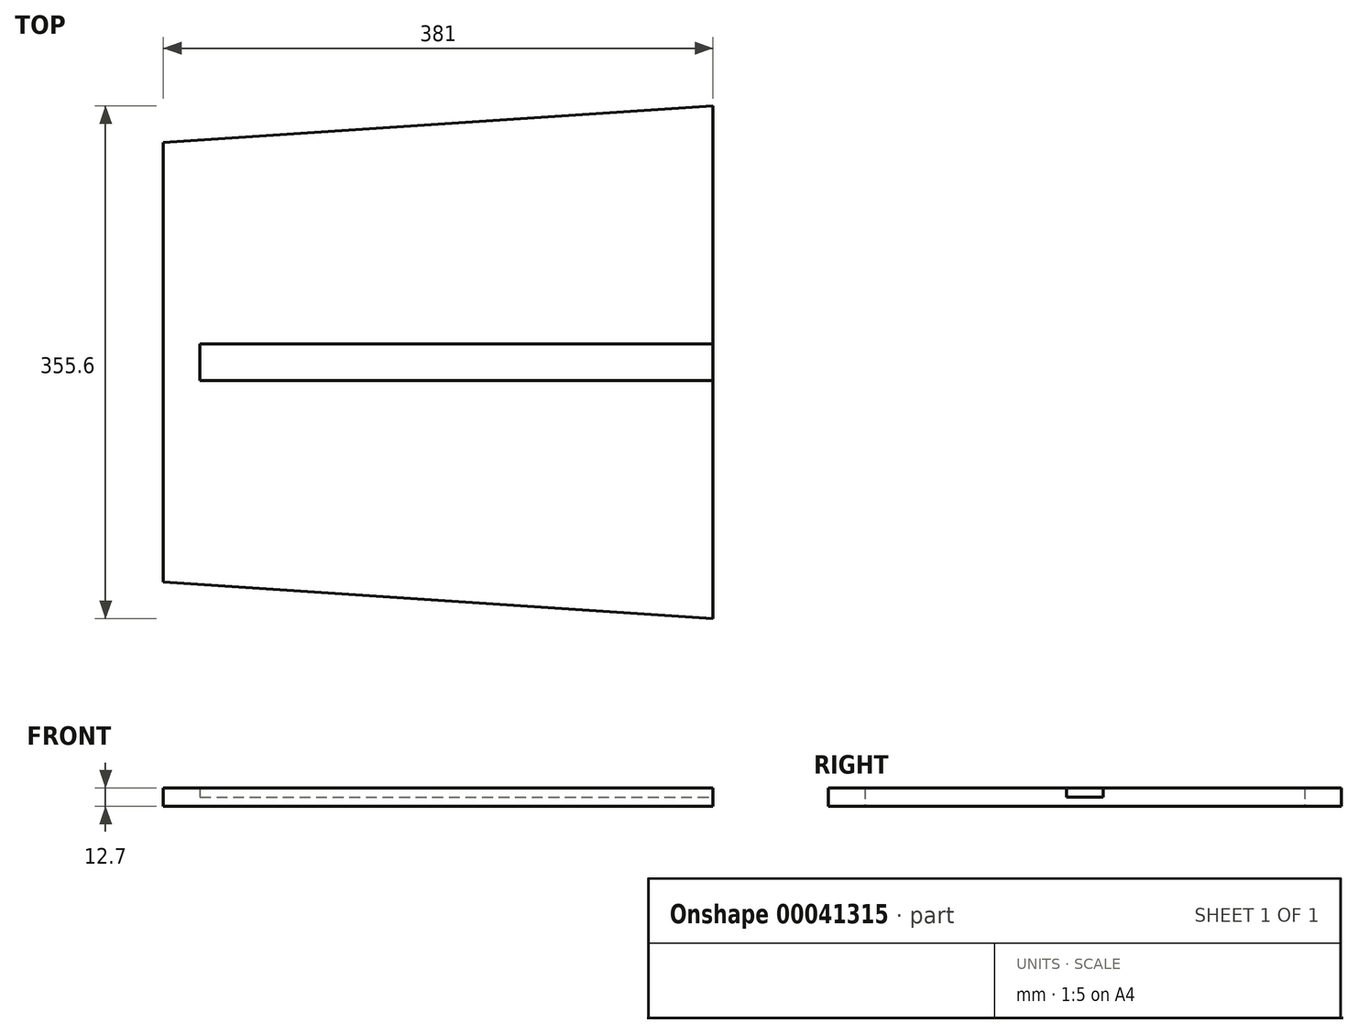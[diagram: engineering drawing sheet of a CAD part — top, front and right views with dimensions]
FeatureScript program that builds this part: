
annotation { "Feature Type Name" : "Feature", "Feature Type Description" : "" }
export const myFeature = defineFeature(function(context is Context, id is Id, definition is map)
    precondition{}
    {
        {
            var Q0;
            Q0=qCreatedBy(makeId("Top.planeOp"),FACE);
            var sketch = newSketch(context, id + "F0", { "sketchPlane" : qUnion([Q0])});
            skLineSegment(sketch, "E0.left", {"start": v(-193.45, -82.1) * mm, "end": v(-193.45, 222.7) * mm});
            skLineSegment(sketch, "E0.right", {"start": v(187.55, -107.5) * mm, "end": v(187.55, 248.1) * mm});
            skLineSegment(sketch, "E1", {"start": v(187.55, -107.5) * mm, "end": v(-193.45, -82.1) * mm});
            skLineSegment(sketch, "E2", {"start": v(187.55, 248.1) * mm, "end": v(-193.45, 222.7) * mm});
            skSolve(sketch);
        }
        {
            var Q0;
            Q0=makeQuery(id+"F0.imprint","IMPRINT",FACE,{"disambiguationData":[TD([[makeQuery(id+"F0.imprint","IMPRINT",EDGE,{"derivedFrom":sQuery(id+"F0.wireOp",EDGE,"E0.left")}),-1.0]])]});
            extrude(context, id + "F1", {"entities" : qUnion([Q0]), "depth" : 6.35 * mm});
        }
        {
            var Q0;
            Q0=makeQuery(id+"F1.opExtrude","CAP_FACE",FACE,{"disambiguationData":[OSD([sQuery(id+"F0.wireOp",EDGE,"E0.left"),sQuery(id+"F0.wireOp",EDGE,"E0.right"),sQuery(id+"F0.wireOp",EDGE,"E1"),sQuery(id+"F0.wireOp",EDGE,"E2")])],"isStart":false});
            var sketch = newSketch(context, id + "F2", { "sketchPlane" : qUnion([Q0])});
            skLineSegment(sketch, "E3.bottom", {"start": v(-168.05, 83) * mm, "end": v(235.06, 83) * mm});
            skLineSegment(sketch, "E3.top", {"start": v(-168.05, 57.6) * mm, "end": v(235.06, 57.6) * mm});
            skLineSegment(sketch, "E3.left", {"start": v(-168.05, 83) * mm, "end": v(-168.05, 57.6) * mm});
            skLineSegment(sketch, "E3.right", {"start": v(235.06, 83) * mm, "end": v(235.06, 57.6) * mm});
            skSolve(sketch);
        }
        {
            var Q0;
            {var subQ5=sQuery(id+"F2.wireOp",EDGE,"E3.left");Q0=makeQuery(id+"F2.imprint","IMPRINT",FACE,{"disambiguationData":[TD([[makeQuery(id+"F2.imprint","IMPRINT",EDGE,{"derivedFrom":subQ5}),-1.0]])]});}
            extrude(context, id + "F3", {"entities" : qUnion([Q0]), "operationType" : NewBodyOperationType.ADD, "depth" : 6.35 * mm});
        }
    });
